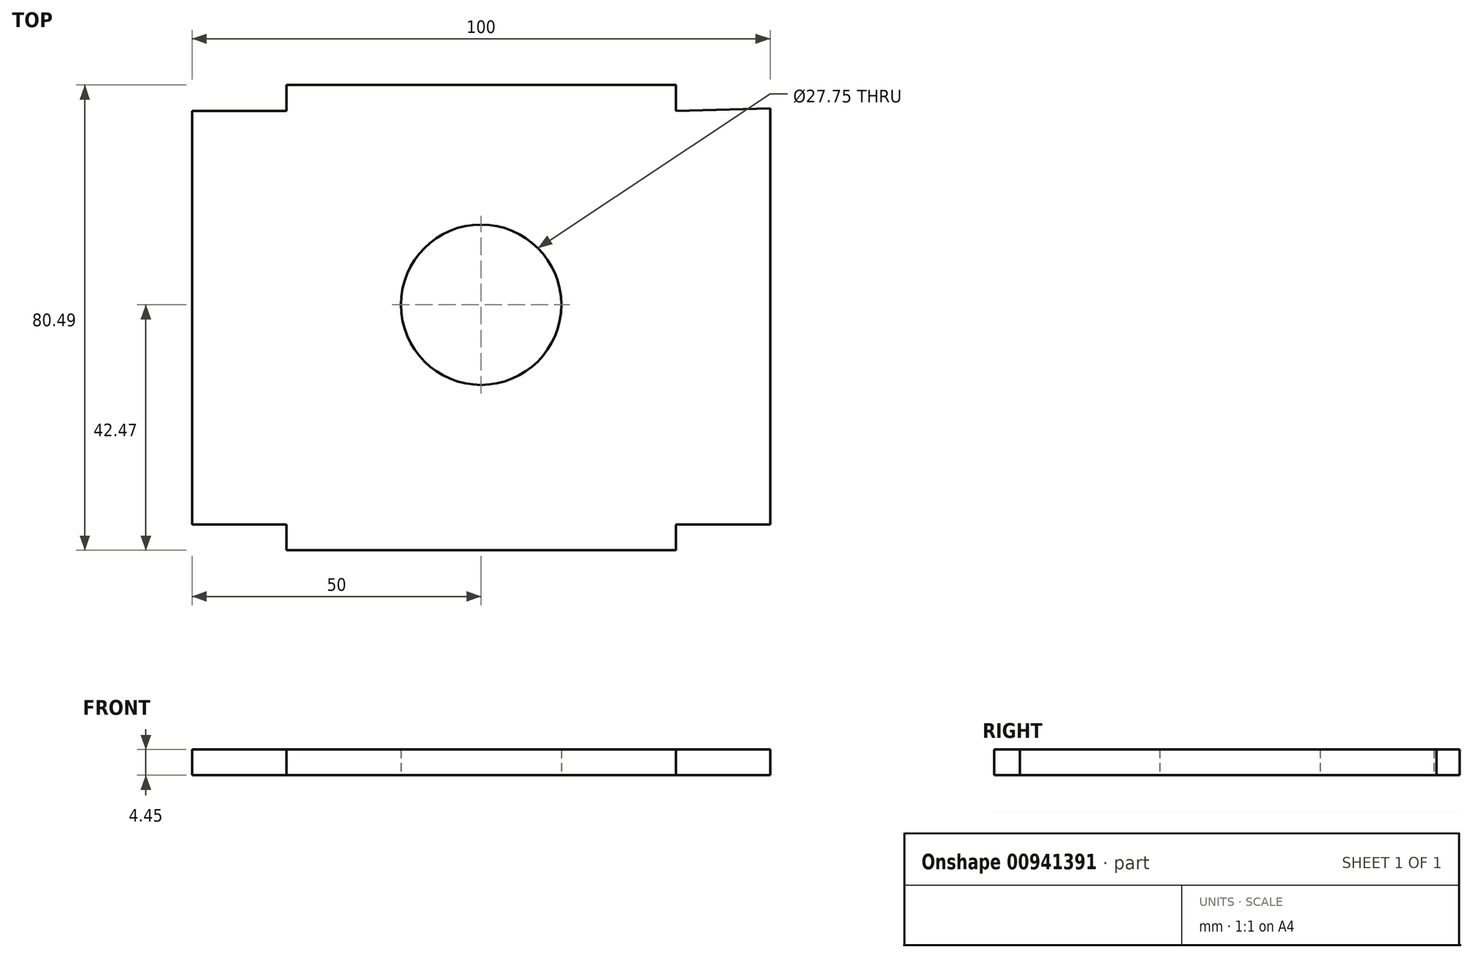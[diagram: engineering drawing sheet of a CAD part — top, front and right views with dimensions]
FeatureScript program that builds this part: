
annotation { "Feature Type Name" : "Feature", "Feature Type Description" : "" }
export const myFeature = defineFeature(function(context is Context, id is Id, definition is map)
    precondition{}
    {
        {
            var Q0;
            Q0=qCreatedBy(makeId("Top.planeOp"),FACE);
            var sketch = newSketch(context, id + "F0", { "sketchPlane" : qUnion([Q0])});
            skLineSegment(sketch, "E0.left", {"start": v(50, -16.64) * mm, "end": v(50, 16.64) * mm});
            skLineSegment(sketch, "E0.right", {"start": v(-50, -33.57) * mm, "end": v(-50, -16.64) * mm});
            skPoint(sketch, "E0.middle", {"position": v(0, 0) * mm});
            skLineSegment(sketch, "E1.right", {"start": v(-33.7, 33.57) * mm, "end": v(-33.7, 38.02) * mm});
            skLineSegment(sketch, "E2.MirrorCS", {"start": v(33.7, 33.57) * mm, "end": v(33.7, 38.02) * mm});
            skLineSegment(sketch, "E3.MirrorCS", {"start": v(50, 33.57) * mm, "end": v(50, 34) * mm});
            skPoint(sketch, "E4.middle", {"position": v(-50, 0) * mm});
            skPoint(sketch, "E5.orphan", {"position": v(-45.55, 16.64) * mm});
            skPoint(sketch, "E6.orphan", {"position": v(-45.55, -16.64) * mm});
            skLineSegment(sketch, "E7.trimOffspring", {"start": v(-50, 16.64) * mm, "end": v(-50, 33.57) * mm});
            skLineSegment(sketch, "E8.MirrorCS", {"start": v(-33.7, 38.02) * mm, "end": v(33.7, 38.02) * mm});
            skPoint(sketch, "E1.left.end.orphan", {"position": v(-50, 38.02) * mm});
            skPoint(sketch, "E9.MirrorCS.end.orphan", {"position": v(33.7, 38.02) * mm});
            skLineSegment(sketch, "E10", {"start": v(-50, 33.57) * mm, "end": v(-33.7, 33.57) * mm});
            skLineSegment(sketch, "E11", {"start": v(33.7, 33.57) * mm, "end": v(50, 34) * mm});
            skLineSegment(sketch, "E12", {"start": v(50, 33.57) * mm, "end": v(50, 16.64) * mm});
            skLineSegment(sketch, "E13", {"start": v(50, -16.64) * mm, "end": v(50, -33.57) * mm});
            skLineSegment(sketch, "E14", {"start": v(-50, -16.64) * mm, "end": v(-50, 16.64) * mm});
            skLineSegment(sketch, "E15.top", {"start": v(33.7, -38.02) * mm, "end": v(50, -38.02) * mm});
            skLineSegment(sketch, "E15.right", {"start": v(50, -33.57) * mm, "end": v(50, -38.02) * mm});
            skLineSegment(sketch, "E16.top", {"start": v(-50, -38.02) * mm, "end": v(-33.7, -38.02) * mm});
            skLineSegment(sketch, "E16.left", {"start": v(-50, -33.57) * mm, "end": v(-50, -38.02) * mm});
            skLineSegment(sketch, "E17.top", {"start": v(-33.7, -42.47) * mm, "end": v(33.7, -42.47) * mm});
            skLineSegment(sketch, "E17.left", {"start": v(-33.7, -38.02) * mm, "end": v(-33.7, -42.47) * mm});
            skLineSegment(sketch, "E17.right", {"start": v(33.7, -38.02) * mm, "end": v(33.7, -42.47) * mm});
            skPoint(sketch, "E18.left.start.orphan", {"position": v(-33.7, -33.57) * mm});
            skPoint(sketch, "E18.top.end.orphan", {"position": v(33.7, -38.02) * mm});
            skCircle(sketch, "E19", {"center": v(0, 0) * mm, "radius": 13.87 * mm});
            skSolve(sketch);
        }
        {
            var Q0;
            Q0=makeQuery(id+"F0.imprint","IMPRINT",FACE,{"disambiguationData":[TD([[makeQuery(id+"F0.imprint","IMPRINT",EDGE,{"derivedFrom":sQuery(id+"F0.wireOp",EDGE,"E0.left")}),1.0]])]});
            extrude(context, id + "F1", {"entities" : qUnion([Q0]), "depth" : 4.45 * mm, "offsetDistance" : 25 * mm});
        }
    });
